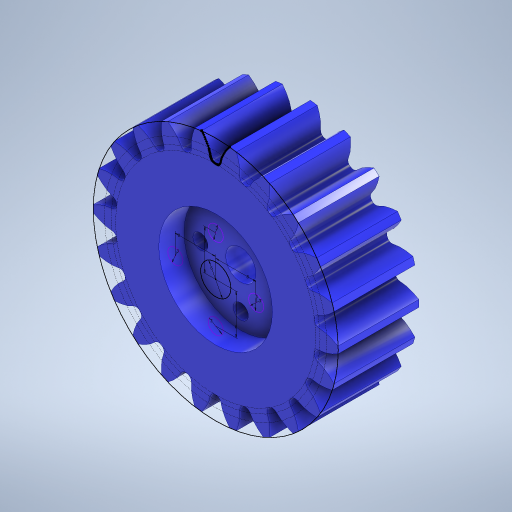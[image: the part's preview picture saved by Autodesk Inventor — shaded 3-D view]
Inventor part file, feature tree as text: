
AUTODESK INVENTOR PART (.ipt)
format: ipt  version: 2024.2 (Build 282272000, 272)  size: 516,608 bytes
history: native  units: mm
features: extrude x6, sketch x5, other x3, pattern_circular x1, loft x1
ambient origin geometry x8: Origin, YZ Plane, XZ Plane, XY Plane, X Axis, Y Axis, Z Axis, Center Point
bodies: Body1 (feature_tree)
feature tree (16):
  other  "Твердое тело1"
  sketch  "Sketch1"  dims[d0=16.0mm d1=0.0mm d4=0.0mm d5=0.0mm d6=220.0mm d7=360.0deg d9=6.0mm d10=3.0mm d11=3.0mm d12=3.0mm d13=3.0mm d14=8.0mm d15=8.0mm d16=8.0mm d17=8.0mm d18=3.0mm d19=10.0mm d20=0.0mm d21=0.0mm d22=3.0mm d23=52.0mm d24=0.0mm d25=90.0deg d26=0.0mm d27=90.0deg d28=22.8mm d29=7.5mm d30=0.0mm d31=3.0mm d32=0.0mm d33=3.0mm d39=22.5mm d40=5.0mm d41=0.0mm]
  extrude  "Выдавливание1"  TaperAngle=0.0deg  [1 undecoded]
  extrude  "Выдавливание2"  TaperAngle=0.0deg  [1 undecoded]
  pattern_circular  "Круговой массив1"  Count=22 Angle=360.0deg
  extrude  "Выдавливание3"  Depth=5.0mm
  other  "РабПлоскость1"
  extrude  "Выдавливание6"  Depth=3.0mm
  loft  "Лофт1"
  extrude  "Выдавливание4"  Depth=3.0mm
  extrude  "Выдавливание5"  Depth=3.0mm
  other  "РабПлоскость2"
  sketch  "Эскиз2"
  sketch  "Эскиз3"
  sketch  "Эскиз4"
  sketch  "Эскиз7"
note: 2 required parameter values undecoded (feature->parameter linkage not recoverable at this tier; creation-order binding heuristic only, values carry confidence <= 0.55)
